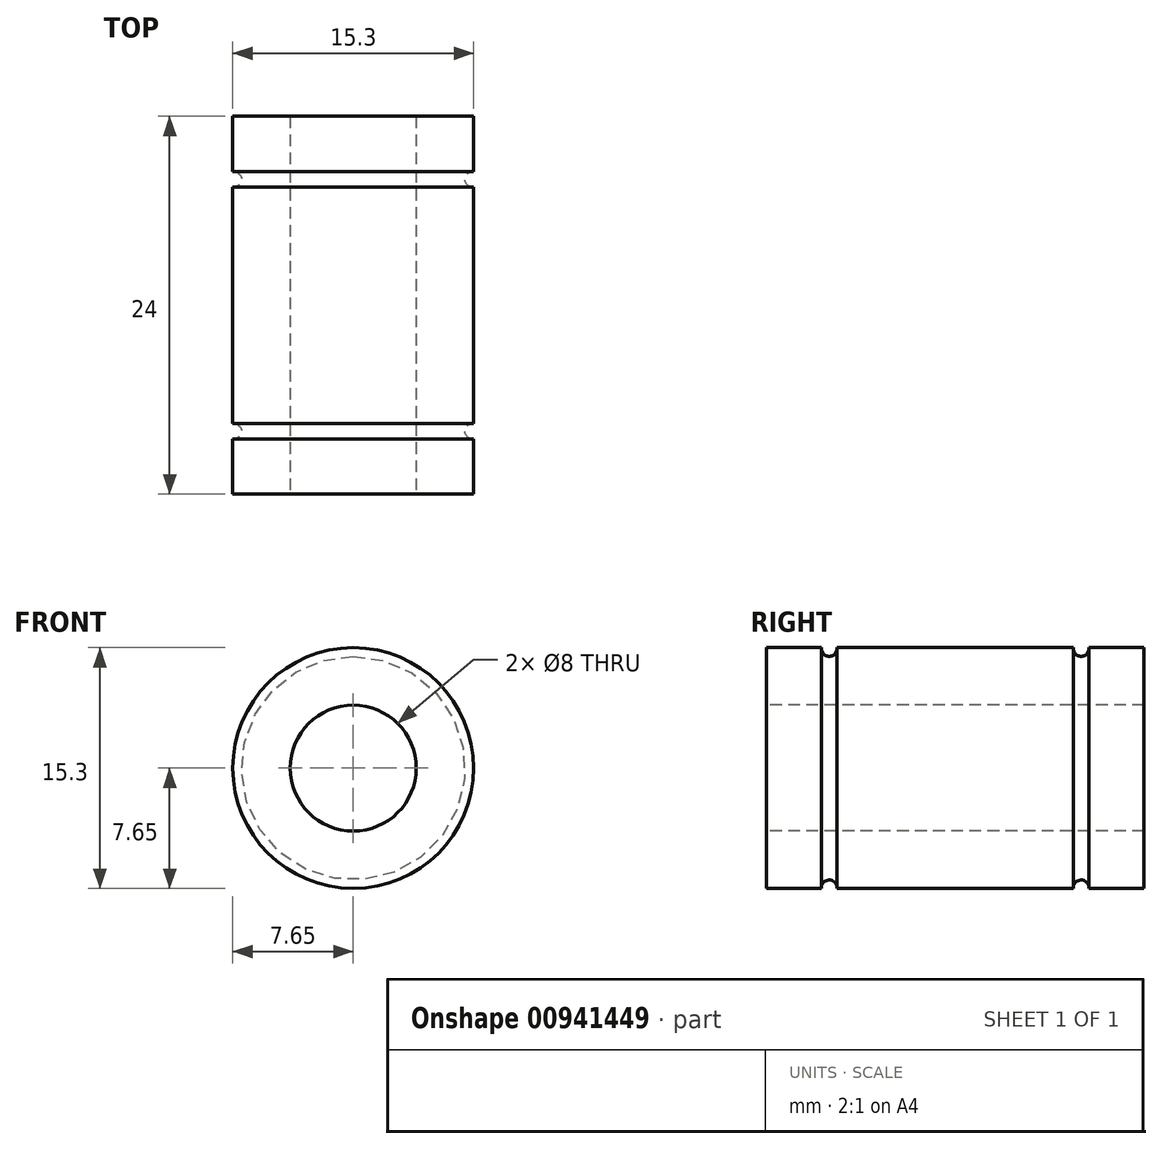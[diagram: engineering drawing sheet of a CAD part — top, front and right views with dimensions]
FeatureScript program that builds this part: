
annotation { "Feature Type Name" : "Feature", "Feature Type Description" : "" }
export const myFeature = defineFeature(function(context is Context, id is Id, definition is map)
    precondition{}
    {
        {
            var Q0;
            Q0=qCreatedBy(makeId("Front.planeOp"),FACE);
            var sketch = newSketch(context, id + "F0", { "sketchPlane" : qUnion([Q0])});
            skCircle(sketch, "E0", {"center": v(0, 0) * mm, "radius": 7.65 * mm});
            skSolve(sketch);
        }
        {
            var Q0;
            Q0=makeQuery(id+"F0.imprint","IMPRINT",FACE,{"disambiguationData":[TD([[makeQuery(id+"F0.imprint","IMPRINT",EDGE,{"derivedFrom":sQuery(id+"F0.wireOp",EDGE,"E0")}),1.0]])]});
            extrude(context, id + "F1", {"entities" : qUnion([Q0]), "depth" : 24 * mm, "offsetDistance" : 25 * mm});
        }
        {
            var Q0;
            Q0=makeQuery(id+"F1.opExtrude","CAP_FACE",FACE,{"disambiguationData":[OSD([sQuery(id+"F0.wireOp",EDGE,"E0")])],"isStart":false});
            var sketch = newSketch(context, id + "F2", { "sketchPlane" : qUnion([Q0])});
            skCircle(sketch, "E1", {"center": v(0, 0) * mm, "radius": 4 * mm});
            skSolve(sketch);
        }
        {
            var Q0;
            Q0=makeQuery(id+"F2.imprint","IMPRINT",FACE,{"disambiguationData":[TD([[makeQuery(id+"F2.imprint","IMPRINT",EDGE,{"derivedFrom":sQuery(id+"F2.wireOp",EDGE,"E1")}),1.0]])]});
            extrude(context, id + "F3", {"entities" : qUnion([Q0]), "operationType" : NewBodyOperationType.REMOVE, "oppositeDirection" : true, "depth" : 25 * mm, "offsetDistance" : 25 * mm});
        }
        {
            var Q0;
            Q0=qCreatedBy(makeId("Right.planeOp"),FACE);
            var sketch = newSketch(context, id + "F4", { "sketchPlane" : qUnion([Q0])});
            skCircle(sketch, "E2", {"center": v(-20, 7.6) * mm, "radius": 0.5 * mm});
            skCircle(sketch, "E3", {"center": v(-4, 7.6) * mm, "radius": 0.5 * mm});
            skSolve(sketch);
        }
        {
            var Q0;
            Q0=qCreatedBy(makeId("Top.planeOp"),FACE);
            var sketch = newSketch(context, id + "F5", { "sketchPlane" : qUnion([Q0])});
            skLineSegment(sketch, "E4", {"start": v(0, -30.75) * mm, "end": v(0, 14.78) * mm, "construction": true});
            skSolve(sketch);
        }
        {
            var Q0;
            Q0=makeQuery(id+"F4.imprint","IMPRINT",FACE,{"disambiguationData":[TD([[makeQuery(id+"F4.imprint","IMPRINT",EDGE,{"derivedFrom":sQuery(id+"F4.wireOp",EDGE,"E2")}),1.0]])]});
            var Q1;
            Q1=makeQuery(id+"F4.imprint","IMPRINT",FACE,{"disambiguationData":[TD([[makeQuery(id+"F4.imprint","IMPRINT",EDGE,{"derivedFrom":sQuery(id+"F4.wireOp",EDGE,"E3")}),1.0]])]});
            var Q2;
            Q2=sQuery(id+"F5.wireOp",EDGE,"E4");
            revolve(context, id + "F6", {"operationType" : NewBodyOperationType.REMOVE, "surfaceOperationType" : NewSurfaceOperationType.NEW, "entities" : qUnion([Q0, Q1]), "axis" : qUnion([Q2]), "revolveType" : RevolveType.FULL, "oppositeDirection" : true});
        }
    });
